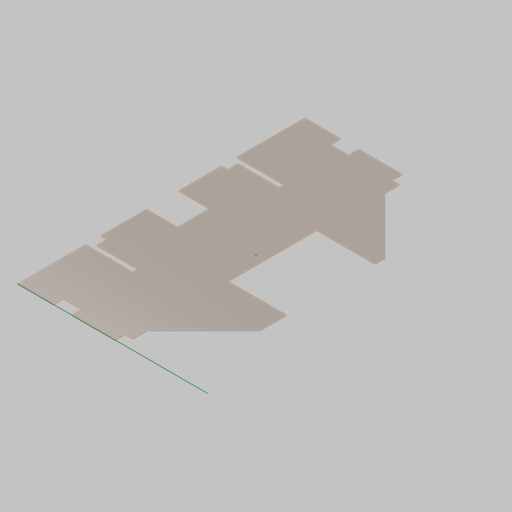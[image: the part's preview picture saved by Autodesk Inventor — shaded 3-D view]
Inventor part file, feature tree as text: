
AUTODESK INVENTOR PART (.ipt)
format: ipt  version: 2023.5 (Build 275446000, 446)  size: 217,600 bytes
history: native  units: in
note: dims shown in document units (in); Inventor stores cm internally (conversion verified against a paired STEP export)
features: sketch x4, other x3, projected_geometry x2, sheet_metal_op x1
ambient origin geometry x8: Origin, YZ Plane, XZ Plane, XY Plane, X Axis, Y Axis, Z Axis, Center Point
bodies: Solid1 (feature_tree)
feature tree (10):
  sheet_metal_op  "Face1"
  sketch  "Sketch3"  dims[d1=28.0in]
  sketch  "Sketch1"  dims[d0=18.5in]
  other  "Plate1"
  sketch  "Sketch4"  dims[d2=0.12in]
  projected_geometry  "Projected Loop1"
  sketch  "Sketch5"  dims[d3=8.25in d4=10.0in d5=45.0deg d6=2.4in d9=2.75in d10=0.12in d11=0.0in d12=45.0deg d13=8.25in d14=9.0in d15=2.75in d16=2.4in d17=6.75in d18=4.5in d19=0.25in d21=4.0in d22=1.0in d23=0.1in d26=5.7in d31=0.5in d32=4.5in d33=6.75in d34=0.25in d35=4.0in d36=1.0in d37=0.1in d38=3.0in d39=1.4in d40=1.7in d41=0.1in d42=1.0in d43=0.75in d44=1.0in d45=0.75in d46=0.75in d47=1.0in d48=0.75in d49=1.0in d50=0.12in d51=0.0in d52=1.75in d53=1.0in d54=3.5in d55=1.75in d56=1.0in d57=3.5in]
  other  "Cut1"
  other  "Cut2"
  projected_geometry  "Project Cut Edges1"
